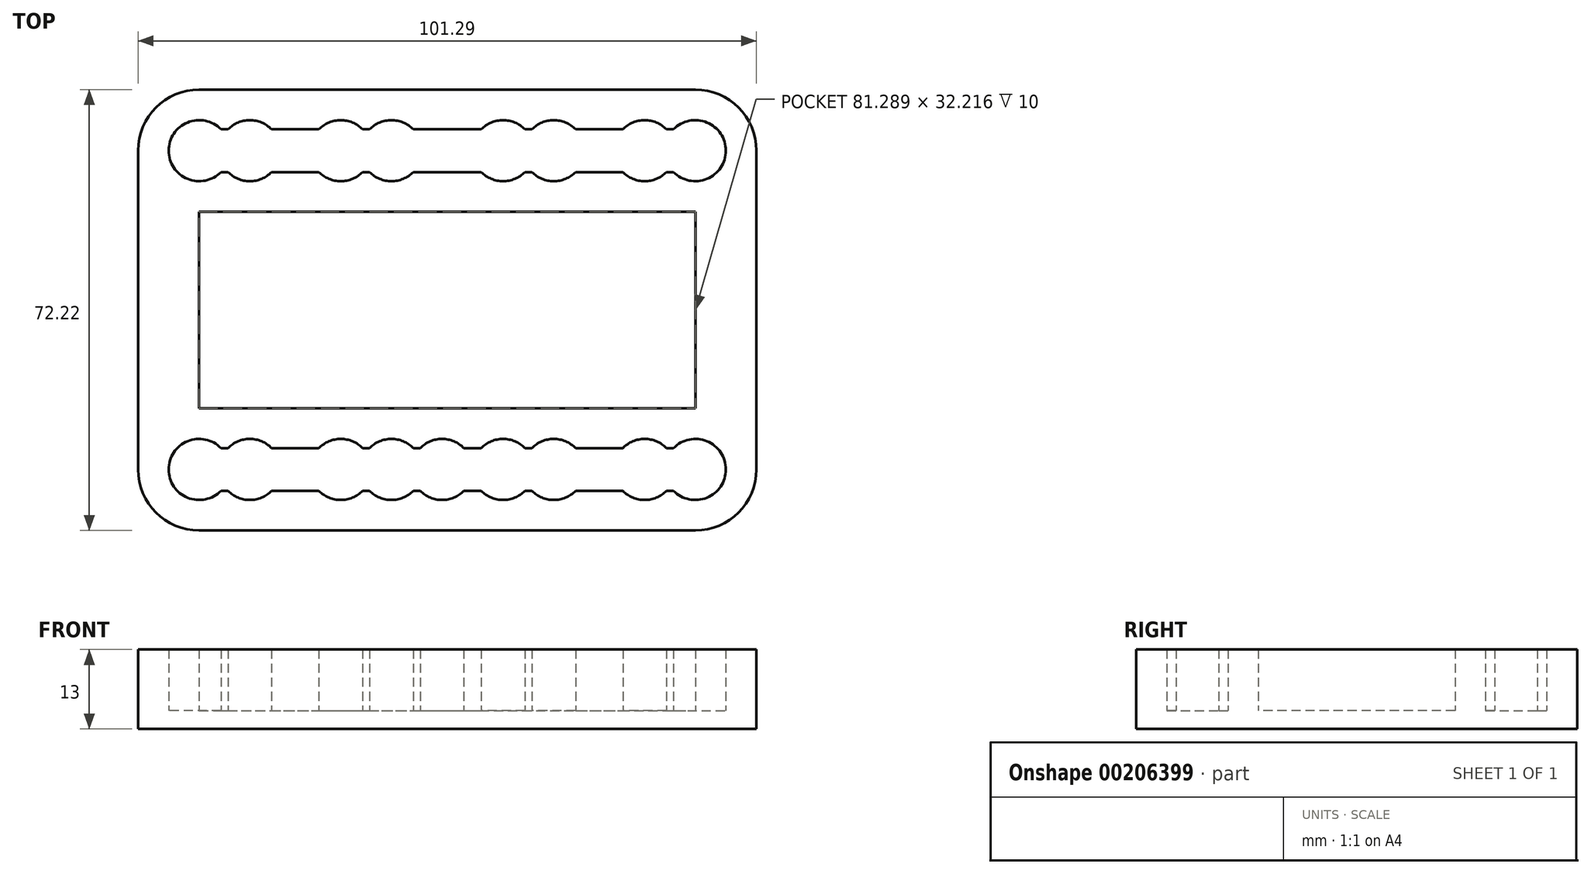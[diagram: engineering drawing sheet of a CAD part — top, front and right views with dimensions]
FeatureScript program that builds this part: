
annotation { "Feature Type Name" : "Feature", "Feature Type Description" : "" }
export const myFeature = defineFeature(function(context is Context, id is Id, definition is map)
    precondition{}
    {
        {
            var Q0;
            Q0=qCreatedBy(makeId("Top.planeOp"),FACE);
            var sketch = newSketch(context, id + "F0", { "sketchPlane" : qUnion([Q0])});
            skCircle(sketch, "E0", {"center": v(0, 0) * mm, "radius": 5 * mm});
            skCircle(sketch, "E1", {"center": v(8.3, 0) * mm, "radius": 5 * mm});
            skCircle(sketch, "E2", {"center": v(23.2, 0) * mm, "radius": 5 * mm});
            skCircle(sketch, "E3", {"center": v(31.5, 0) * mm, "radius": 5 * mm});
            skCircle(sketch, "E4", {"center": v(49.8, 0) * mm, "radius": 5 * mm});
            skCircle(sketch, "E5", {"center": v(58.1, 0) * mm, "radius": 5 * mm});
            skCircle(sketch, "E6", {"center": v(72.99, 0) * mm, "radius": 5 * mm});
            skCircle(sketch, "E7", {"center": v(81.29, 0) * mm, "radius": 5 * mm});
            skLineSegment(sketch, "E8", {"start": v(-18.48, -26.1) * mm, "end": v(129.7, -26.1) * mm, "construction": true});
            skCircle(sketch, "E9.MirrorC", {"center": v(0, -52.22) * mm, "radius": 5 * mm});
            skCircle(sketch, "E10.MirrorC", {"center": v(8.3, -52.22) * mm, "radius": 5 * mm});
            skCircle(sketch, "E11.MirrorC", {"center": v(23.2, -52.22) * mm, "radius": 5 * mm});
            skCircle(sketch, "E12.MirrorC", {"center": v(31.5, -52.22) * mm, "radius": 5 * mm});
            skArc(sketch, "E13.MirrorC", {"start": v(46.22, -48.72) * mm, "mid": v(54.8, -52.22) * mm, "end": v(46.22, -55.72) * mm});
            skCircle(sketch, "E14.MirrorC", {"center": v(58.1, -52.22) * mm, "radius": 5 * mm});
            skCircle(sketch, "E15.MirrorC", {"center": v(72.99, -52.22) * mm, "radius": 5 * mm});
            skCircle(sketch, "E16.MirrorC", {"center": v(81.29, -52.22) * mm, "radius": 5 * mm});
            skLineSegment(sketch, "E17.bottom", {"start": v(0, 10) * mm, "end": v(81.29, 10) * mm});
            skLineSegment(sketch, "E17.left", {"start": v(-10, 0) * mm, "end": v(-10, -26.1) * mm});
            skLineSegment(sketch, "E17.right", {"start": v(91.29, 0) * mm, "end": v(91.29, -26.1) * mm});
            skLineSegment(sketch, "E18.MirrorCS", {"start": v(-10, -52.22) * mm, "end": v(-10, -26.1) * mm});
            skLineSegment(sketch, "E19.MirrorCS", {"start": v(0, -62.22) * mm, "end": v(81.29, -62.22) * mm});
            skLineSegment(sketch, "E20.MirrorCS", {"start": v(91.29, -52.22) * mm, "end": v(91.29, -26.1) * mm});
            skLineSegment(sketch, "E21", {"start": v(0, -26.1) * mm, "end": v(0, -10) * mm});
            skLineSegment(sketch, "E22", {"start": v(0, -10) * mm, "end": v(81.29, -10) * mm});
            skLineSegment(sketch, "E23", {"start": v(81.29, -10) * mm, "end": v(81.29, -26.1) * mm});
            skLineSegment(sketch, "E24.MirrorCS", {"start": v(0, -26.1) * mm, "end": v(0, -42.22) * mm});
            skLineSegment(sketch, "E25.MirrorCS", {"start": v(0, -42.22) * mm, "end": v(81.29, -42.22) * mm});
            skLineSegment(sketch, "E26.MirrorCS", {"start": v(81.29, -42.22) * mm, "end": v(81.29, -26.1) * mm});
            skPoint(sketch, "E27.visualSharp", {"position": v(-10, 10) * mm});
            skArc(sketch, "E27.filletArc", {"start": v(0, 10) * mm, "mid": v(-7.07, 7.07) * mm, "end": v(-10, 0) * mm});
            skPoint(sketch, "E28.visualSharp", {"position": v(91.29, 10) * mm});
            skArc(sketch, "E28.filletArc", {"start": v(91.29, 0) * mm, "mid": v(88.36, 7.07) * mm, "end": v(81.29, 10) * mm});
            skPoint(sketch, "E29.visualSharp", {"position": v(91.29, -62.22) * mm});
            skArc(sketch, "E29.filletArc", {"start": v(81.29, -62.22) * mm, "mid": v(88.36, -59.29) * mm, "end": v(91.29, -52.22) * mm});
            skPoint(sketch, "E30.visualSharp", {"position": v(-10, -62.22) * mm});
            skArc(sketch, "E30.filletArc", {"start": v(-10, -52.22) * mm, "mid": v(-7.07, -59.29) * mm, "end": v(0, -62.22) * mm});
            skArc(sketch, "E31", {"start": v(43.36, -48.72) * mm, "mid": v(34.8, -52.22) * mm, "end": v(43.36, -55.72) * mm});
            skLineSegment(sketch, "E32", {"start": v(0, 3.5) * mm, "end": v(81.29, 3.5) * mm});
            skLineSegment(sketch, "E33", {"start": v(0, 3.5) * mm, "end": v(0, 0) * mm});
            skLineSegment(sketch, "E34", {"start": v(81.29, 3.5) * mm, "end": v(81.29, 0) * mm});
            skLineSegment(sketch, "E35.MirrorCS", {"start": v(81.29, -3.5) * mm, "end": v(81.29, 0) * mm});
            skLineSegment(sketch, "E36.MirrorCS", {"start": v(0, -3.5) * mm, "end": v(81.29, -3.5) * mm});
            skLineSegment(sketch, "E37.MirrorCS", {"start": v(0, -3.5) * mm, "end": v(0, 0) * mm});
            skLineSegment(sketch, "E38.MirrorCS", {"start": v(0, -48.72) * mm, "end": v(0, -52.22) * mm});
            skLineSegment(sketch, "E39.MirrorCS", {"start": v(0, -55.72) * mm, "end": v(0, -52.22) * mm});
            skLineSegment(sketch, "E40.MirrorCS", {"start": v(0, -55.72) * mm, "end": v(81.29, -55.72) * mm});
            skLineSegment(sketch, "E41.MirrorCS", {"start": v(0, -48.72) * mm, "end": v(81.29, -48.72) * mm});
            skLineSegment(sketch, "E42.MirrorCS", {"start": v(81.29, -55.72) * mm, "end": v(81.29, -52.22) * mm});
            skLineSegment(sketch, "E43.MirrorCS", {"start": v(81.29, -48.72) * mm, "end": v(81.29, -52.22) * mm});
            skSolve(sketch);
        }
        {
            var Q0;
            Q0 = qSketchRegion(id + "F0", true);
            extrude(context, id + "F1", {"entities" : qUnion([Q0]), "depth" : 10 * mm});
        }
        {
            var Q0;
            Q0=makeQuery(id+"F1.opExtrude","CAP_FACE",FACE,{"disambiguationData":[OSD([sQuery(id+"F0.wireOp",EDGE,"E0"),sQuery(id+"F0.wireOp",EDGE,"E1"),sQuery(id+"F0.wireOp",EDGE,"E2"),sQuery(id+"F0.wireOp",EDGE,"E3"),sQuery(id+"F0.wireOp",EDGE,"E4"),sQuery(id+"F0.wireOp",EDGE,"E5"),sQuery(id+"F0.wireOp",EDGE,"E6"),sQuery(id+"F0.wireOp",EDGE,"E7"),sQuery(id+"F0.wireOp",EDGE,"E9.MirrorC"),sQuery(id+"F0.wireOp",EDGE,"E10.MirrorC"),sQuery(id+"F0.wireOp",EDGE,"E11.MirrorC"),sQuery(id+"F0.wireOp",EDGE,"E12.MirrorC"),sQuery(id+"F0.wireOp",EDGE,"E13.MirrorC"),sQuery(id+"F0.wireOp",EDGE,"E14.MirrorC"),sQuery(id+"F0.wireOp",EDGE,"E15.MirrorC"),sQuery(id+"F0.wireOp",EDGE,"E16.MirrorC"),sQuery(id+"F0.wireOp",EDGE,"E17.bottom"),sQuery(id+"F0.wireOp",EDGE,"E17.left"),sQuery(id+"F0.wireOp",EDGE,"E17.right"),sQuery(id+"F0.wireOp",EDGE,"E18.MirrorCS"),sQuery(id+"F0.wireOp",EDGE,"E19.MirrorCS"),sQuery(id+"F0.wireOp",EDGE,"E20.MirrorCS"),sQuery(id+"F0.wireOp",EDGE,"E21"),sQuery(id+"F0.wireOp",EDGE,"E22"),sQuery(id+"F0.wireOp",EDGE,"E23"),sQuery(id+"F0.wireOp",EDGE,"E24.MirrorCS"),sQuery(id+"F0.wireOp",EDGE,"E25.MirrorCS"),sQuery(id+"F0.wireOp",EDGE,"E26.MirrorCS"),sQuery(id+"F0.wireOp",EDGE,"E27.filletArc"),sQuery(id+"F0.wireOp",EDGE,"E28.filletArc"),sQuery(id+"F0.wireOp",EDGE,"E29.filletArc"),sQuery(id+"F0.wireOp",EDGE,"E30.filletArc"),sQuery(id+"F0.wireOp",EDGE,"E31"),sQuery(id+"F0.wireOp",EDGE,"E32"),sQuery(id+"F0.wireOp",EDGE,"E36.MirrorCS"),sQuery(id+"F0.wireOp",EDGE,"E40.MirrorCS"),sQuery(id+"F0.wireOp",EDGE,"E41.MirrorCS")])],"isStart":true});
            var sketch = newSketch(context, id + "F2", { "sketchPlane" : qUnion([Q0])});
            skLineSegment(sketch, "E44", {"start": v(-10, 52.22) * mm, "end": v(-10, 0) * mm});
            skLineSegment(sketch, "E45", {"start": v(0, -10) * mm, "end": v(81.29, -10) * mm});
            skLineSegment(sketch, "E46", {"start": v(91.29, 0) * mm, "end": v(91.29, 52.22) * mm});
            skLineSegment(sketch, "E47", {"start": v(81.29, 62.22) * mm, "end": v(0, 62.22) * mm});
            skArc(sketch, "E48", {"start": v(-10, 52.22) * mm, "mid": v(-7.07, 59.29) * mm, "end": v(0, 62.22) * mm});
            skArc(sketch, "E49", {"start": v(81.29, 62.22) * mm, "mid": v(88.36, 59.29) * mm, "end": v(91.29, 52.22) * mm});
            skArc(sketch, "E50", {"start": v(91.29, 0) * mm, "mid": v(88.36, -7.07) * mm, "end": v(81.29, -10) * mm});
            skArc(sketch, "E51", {"start": v(0, -10) * mm, "mid": v(-7.07, -7.07) * mm, "end": v(-10, 0) * mm});
            skSolve(sketch);
        }
        {
            var Q0;
            Q0 = qSketchRegion(id + "F2", true);
            extrude(context, id + "F3", {"entities" : qUnion([Q0]), "operationType" : NewBodyOperationType.ADD, "depth" : 3 * mm});
        }
    });
